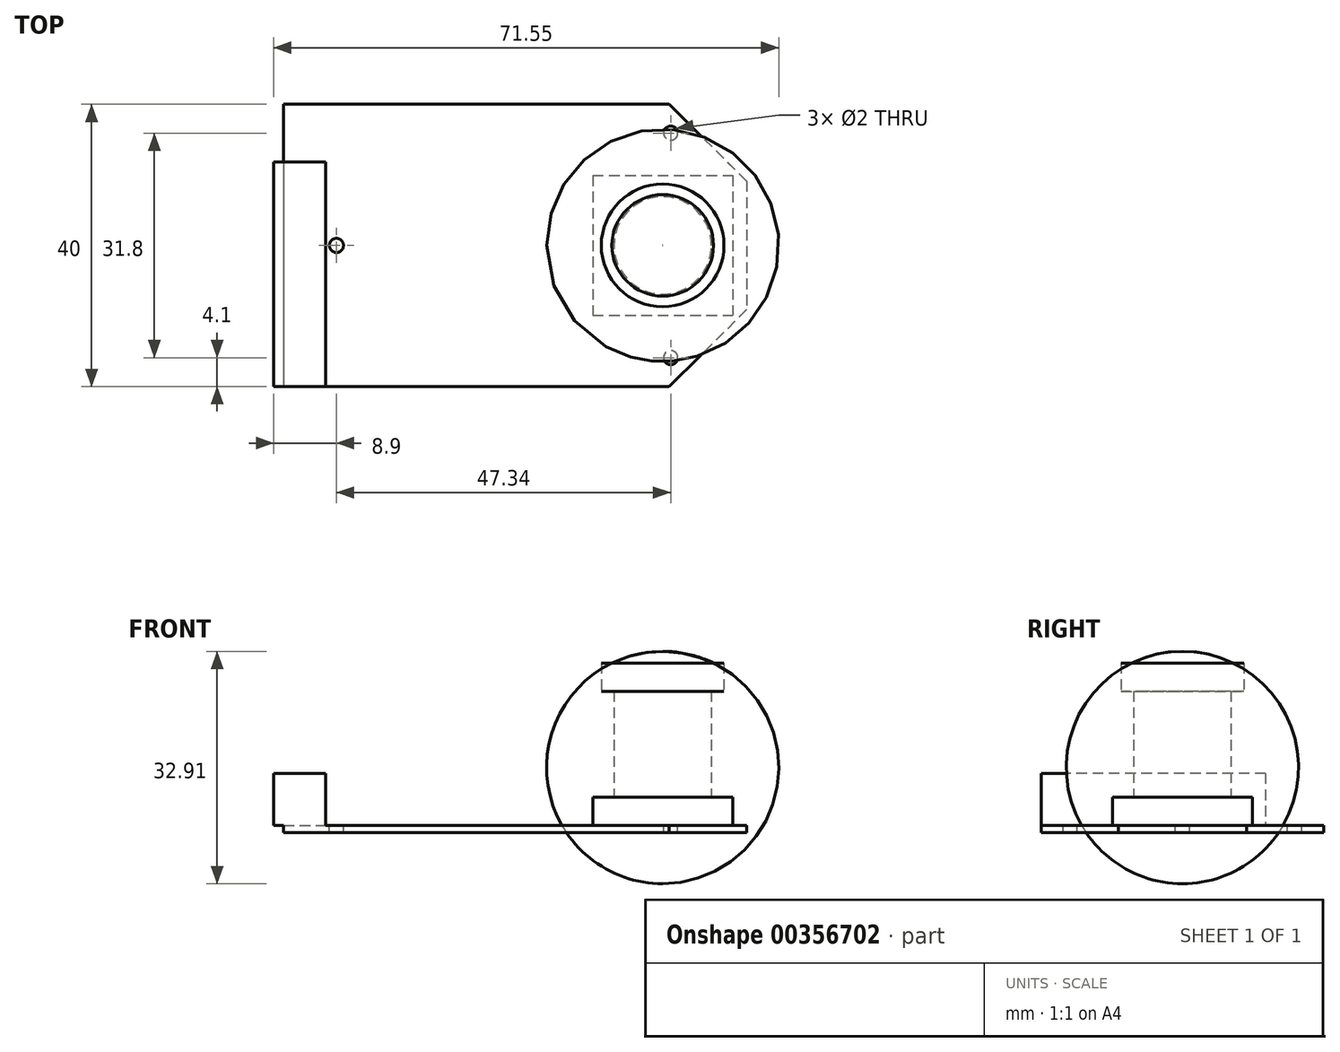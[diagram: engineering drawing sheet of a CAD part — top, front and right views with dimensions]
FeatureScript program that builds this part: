
annotation { "Feature Type Name" : "Feature", "Feature Type Description" : "" }
export const myFeature = defineFeature(function(context is Context, id is Id, definition is map)
    precondition{}
    {
        {
            var Q0;
            Q0=qCreatedBy(makeId("Top.planeOp"),FACE);
            var sketch = newSketch(context, id + "F0", { "sketchPlane" : qUnion([Q0])});
            skLineSegment(sketch, "E0", {"start": v(-32.8, 20) * mm, "end": v(21.8, 20) * mm});
            skLineSegment(sketch, "E1", {"start": v(-32.8, 20) * mm, "end": v(-32.8, -20) * mm});
            skLineSegment(sketch, "E2", {"start": v(-32.8, -20) * mm, "end": v(21.8, -20) * mm});
            skLineSegment(sketch, "E3", {"start": v(32.8, 9.1) * mm, "end": v(32.8, -9.1) * mm});
            skLineSegment(sketch, "E4", {"start": v(32.8, -9.1) * mm, "end": v(21.8, -20) * mm});
            skLineSegment(sketch, "E5", {"start": v(32.8, 9.1) * mm, "end": v(21.8, 20) * mm});
            skSolve(sketch);
        }
        {
            var Q0;
            Q0=makeQuery(id+"F0.imprint","IMPRINT",FACE,{"disambiguationData":[TD([[makeQuery(id+"F0.imprint","IMPRINT",EDGE,{"derivedFrom":sQuery(id+"F0.wireOp",EDGE,"E0")}),-1.0]])]});
            extrude(context, id + "F1", {"entities" : qUnion([Q0]), "depth" : 1 * mm});
        }
        {
            var Q0;
            Q0=makeQuery(id+"F1.opExtrude","CAP_FACE",FACE,{"disambiguationData":[OSD([sQuery(id+"F0.wireOp",EDGE,"E0"),sQuery(id+"F0.wireOp",EDGE,"E1"),sQuery(id+"F0.wireOp",EDGE,"E2"),sQuery(id+"F0.wireOp",EDGE,"E3"),sQuery(id+"F0.wireOp",EDGE,"E4"),sQuery(id+"F0.wireOp",EDGE,"E5")])],"isStart":false});
            var sketch = newSketch(context, id + "F2", { "sketchPlane" : qUnion([Q0])});
            skLineSegment(sketch, "E6.bottom", {"start": v(11, 9.9) * mm, "end": v(30.8, 9.9) * mm});
            skLineSegment(sketch, "E6.top", {"start": v(11, -9.9) * mm, "end": v(30.8, -9.9) * mm});
            skLineSegment(sketch, "E6.left", {"start": v(11, 9.9) * mm, "end": v(11, -9.9) * mm});
            skLineSegment(sketch, "E6.right", {"start": v(30.8, 9.9) * mm, "end": v(30.8, -9.9) * mm});
            skSolve(sketch);
        }
        {
            var Q0;
            Q0=makeQuery(id+"F2.imprint","IMPRINT",FACE,{"disambiguationData":[TD([[makeQuery(id+"F2.imprint","IMPRINT",EDGE,{"derivedFrom":sQuery(id+"F2.wireOp",EDGE,"E6.bottom")}),-1.0]])]});
            extrude(context, id + "F3", {"entities" : qUnion([Q0]), "operationType" : NewBodyOperationType.ADD, "depth" : 4 * mm});
        }
        {
            var Q0;
            Q0=makeQuery(id+"F3.opExtrude","CAP_FACE",FACE,{"disambiguationData":[OSD([sQuery(id+"F2.wireOp",EDGE,"E6.bottom"),sQuery(id+"F2.wireOp",EDGE,"E6.top"),sQuery(id+"F2.wireOp",EDGE,"E6.left"),sQuery(id+"F2.wireOp",EDGE,"E6.right")])],"isStart":false});
            var sketch = newSketch(context, id + "F4", { "sketchPlane" : qUnion([Q0])});
            skCircle(sketch, "E7", {"center": v(20.9, 0) * mm, "radius": 6.9 * mm});
            skPoint(sketch, "E7.centerSnap0", {"position": v(20.9, -9.9) * mm});
            skSolve(sketch);
        }
        {
            var Q0;
            Q0=makeQuery(id+"F4.imprint","IMPRINT",FACE,{"disambiguationData":[TD([[makeQuery(id+"F4.imprint","IMPRINT",EDGE,{"derivedFrom":sQuery(id+"F4.wireOp",EDGE,"E7")}),1.0]])]});
            extrude(context, id + "F5", {"entities" : qUnion([Q0]), "operationType" : NewBodyOperationType.ADD, "depth" : 15 * mm});
        }
        {
            var Q0;
            Q0=makeQuery(id+"F5.opExtrude","CAP_FACE",FACE,{"disambiguationData":[OSD([sQuery(id+"F4.wireOp",EDGE,"E7")])],"isStart":false});
            var sketch = newSketch(context, id + "F6", { "sketchPlane" : qUnion([Q0])});
            skCircle(sketch, "E8", {"center": v(20.9, 0) * mm, "radius": 8.7 * mm});
            skSolve(sketch);
        }
        {
            var Q0;
            Q0=makeQuery(id+"F6.imprint","IMPRINT",FACE,{"disambiguationData":[TD([[makeQuery(id+"F6.imprint","IMPRINT",EDGE,{"derivedFrom":sQuery(id+"F6.wireOp",EDGE,"E8")}),1.0]])]});
            var Q1;
            Q1=makeQuery(id+"F6.imprint","IMPRINT",FACE,{"disambiguationData":[TD([[makeQuery(id+"F6.imprint","IMPRINT",EDGE,{"derivedFrom":makeQuery(id+"F5.opExtrude","CAP_EDGE",EDGE,{"disambiguationData":[OSD([sQuery(id+"F4.wireOp",EDGE,"E7")])],"isStart":false})}),1.0]])]});
            extrude(context, id + "F7", {"entities" : qUnion([Q0, Q1]), "operationType" : NewBodyOperationType.ADD, "depth" : 4 * mm});
        }
        {
            var Q0;
            Q0=makeQuery(id+"F1.opExtrude","CAP_FACE",FACE,{"disambiguationData":[OSD([sQuery(id+"F0.wireOp",EDGE,"E0"),sQuery(id+"F0.wireOp",EDGE,"E1"),sQuery(id+"F0.wireOp",EDGE,"E2"),sQuery(id+"F0.wireOp",EDGE,"E3"),sQuery(id+"F0.wireOp",EDGE,"E4"),sQuery(id+"F0.wireOp",EDGE,"E5")])],"isStart":false});
            var sketch = newSketch(context, id + "F8", { "sketchPlane" : qUnion([Q0])});
            skLineSegment(sketch, "E9.bottom", {"start": v(-34.2, 11.8) * mm, "end": v(-26.85, 11.8) * mm});
            skLineSegment(sketch, "E9.top", {"start": v(-34.2, -20) * mm, "end": v(-26.85, -20) * mm});
            skLineSegment(sketch, "E9.left", {"start": v(-34.2, 11.8) * mm, "end": v(-34.2, -20) * mm});
            skLineSegment(sketch, "E9.right", {"start": v(-26.85, 11.8) * mm, "end": v(-26.85, -20) * mm});
            skSolve(sketch);
        }
        {
            var Q0;
            {var subQ0=sQuery(id+"F8.wireOp",EDGE,"E9.left");Q0=makeQuery(id+"F8.imprint","IMPRINT",FACE,{"disambiguationData":[TD([[makeQuery(id+"F8.imprint","IMPRINT",EDGE,{"derivedFrom":subQ0}),1.0]])]});}
            var Q1;
            {var subQ0=sQuery(id+"F8.wireOp",EDGE,"E9.right");Q1=makeQuery(id+"F8.imprint","IMPRINT",FACE,{"disambiguationData":[TD([[makeQuery(id+"F8.imprint","IMPRINT",EDGE,{"derivedFrom":subQ0}),-1.0]])]});}
            extrude(context, id + "F9", {"entities" : qUnion([Q0, Q1]), "operationType" : NewBodyOperationType.ADD, "depth" : 7.37 * mm});
        }
        {
            var Q0;
            Q0=makeQuery(id+"F1.opExtrude","CAP_FACE",FACE,{"disambiguationData":[OSD([sQuery(id+"F0.wireOp",EDGE,"E0"),sQuery(id+"F0.wireOp",EDGE,"E1"),sQuery(id+"F0.wireOp",EDGE,"E2"),sQuery(id+"F0.wireOp",EDGE,"E3"),sQuery(id+"F0.wireOp",EDGE,"E4"),sQuery(id+"F0.wireOp",EDGE,"E5")])],"isStart":false});
            var sketch = newSketch(context, id + "F10", { "sketchPlane" : qUnion([Q0])});
            skCircle(sketch, "E10", {"center": v(-25.3, 0) * mm, "radius": 1 * mm});
            skPoint(sketch, "E10.centerSnap0", {"position": v(-26.85, -4.1) * mm});
            skCircle(sketch, "E11", {"center": v(22.04, 15.9) * mm, "radius": 1 * mm});
            skCircle(sketch, "E12", {"center": v(22.04, -15.9) * mm, "radius": 1 * mm});
            skSolve(sketch);
        }
        {
            var Q0;
            Q0=qSketchRegion(id+"F10",true);
            extrude(context, id + "F11", {"entities" : qUnion([Q0]), "operationType" : NewBodyOperationType.REMOVE, "oppositeDirection" : true, "depth" : 25 * mm});
        }
        {
            var Q0;
            Q0=qCreatedBy(makeId("Front.planeOp"),FACE);
            var sketch = newSketch(context, id + "F12", { "sketchPlane" : qUnion([Q0])});
            skLineSegment(sketch, "E13.0", {"start": v(20.9, 24) * mm, "end": v(28.09, 24) * mm});
            skLineSegment(sketch, "E14", {"start": v(20.9, 49.83) * mm, "end": v(20.9, -46.84) * mm, "construction": true});
            skPoint(sketch, "E15.orphan", {"position": v(12.2, 24) * mm});
            skLineSegment(sketch, "E16", {"start": v(20.9, 25.65) * mm, "end": v(20.9, 24) * mm});
            skArc(sketch, "E17", {"start": v(28.09, 24) * mm, "mid": v(24.59, 25.23) * mm, "end": v(20.9, 25.65) * mm});
            skPoint(sketch, "E18.orphan", {"position": v(29.59, 24) * mm});
            skSolve(sketch);
        }
        {
            var Q0;
            Q0=makeQuery(id+"F12.imprint","IMPRINT",FACE,{"disambiguationData":[TD([[makeQuery(id+"F12.imprint","IMPRINT",EDGE,{"derivedFrom":sQuery(id+"F12.wireOp",EDGE,"E13.0")}),1.0]])]});
            var Q1;
            Q1=sQuery(id+"F12.wireOp",EDGE,"E14");
            revolve(context, id + "F13", {"operationType" : NewBodyOperationType.ADD, "entities" : qUnion([Q0]), "axis" : qUnion([Q1]), "revolveType" : RevolveType.FULL});
        }
    });
